# Revit family: xxxBasin-Ligature_Resistant-Whitehall-Corterra-WH3745
name_source: partatom
category: Plumbing Fixtures
units: mm (PartAtom-declared; Revit-internal decimal feet)

## family parameters
Cut with Voids When Loaded = No
Host = Face
OmniClass Number = 23.45.05.14.14
OmniClass Title = Sinks/Lavatories
Part Type = Normal
Room Calculation Point = No
Round Connector Dimension = Use Diameter
Shared = Yes

## types (1)
- WH3745
    6" Centreset = No
    8" Centreset = Yes
    Assembly Code = D2010310
    CW Connection = Yes
    CWFU = 1.5
    Centerset/2 = 4"
    Cold Water Connection Diameter = 1/2"
    Compliance Certifications = ANSI Z124.3, ANSI Z124.6 and ANSI/ICPA SS-1
    Default Elevation = 0"
    Description = Whitehall Ligature Resistant Corterra Compact Basin
    Faucet Centreset = 8"
    Finish = Corterra Polymer-Whitehall-OCC11M-Blanco Gloss
    Finish - Sink Enclosure = Stailess Steel-Whitehall-EG26-Matte White
    HW Connection = Yes
    HWFU = 1.5
    Height = 20 3/4"
    Hot Water Connection Diameter = 1/2"
    Installation Instruction Link = https://www.whitehallmfg.com
    Installation Type = Wall Mounted
    Length = 15"
    Manufacturer = Whitehall
    Material = Corterra Polymer-Whitehall-OCC11M-Blanco Gloss
    Model = WH3745
    Operating Pressure = 30 PSI to 100 PSI
    Price = Prices may vary. Please consult Manufacturer Representative for most up-to-date price list.
    Product Documentation Link = www.whitehallmfg.com/uploads/fileLibrary/WH3745.pdf
    Product Page URL = https://www.whitehallmfg.com
    URL = https://www.whitehallmfg.com
    Vent Connection = No
    WFU = 2
    WH3376C-WSF Ligature Resistant Faucet with Air-Control Valve Assy Single Temp = No
    WH3377C-WSF Ligature Resistant Faucet with Air-Control Valve Assy Hot & Cold = Yes
    Waste Connection = Yes
    Waste Connection Diameter = 1 1/2"
    Width = 20 1/4"

## geometry (parser evidence)
native form markers: Sweep x3
no freeform markers — native parametric forms only
